annotation { "Feature Type Name" : "Feature", "Feature Type Description" : "" }
export const myFeature = defineFeature(function(context is Context, id is Id, definition is map)
    precondition{}
    {
        {
            var Q0;
            Q0=qCreatedBy(makeId("Top.planeOp"),FACE);
            var sketch = newSketch(context, id + "F0", { "sketchPlane" : qUnion([Q0])});
            skLineSegment(sketch, "E0.bottom", {"start": v(60, 20) * mm, "end": v(-60, 20) * mm});
            skLineSegment(sketch, "E0.top", {"start": v(60, -20) * mm, "end": v(-60, -20) * mm});
            skLineSegment(sketch, "E0.left", {"start": v(60, 20) * mm, "end": v(60, -20) * mm});
            skLineSegment(sketch, "E0.right", {"start": v(-60, 20) * mm, "end": v(-60, -20) * mm});
            skPoint(sketch, "E0.middle", {"position": v(0, 0) * mm});
            skText(sketch, "E1", { "text": "Ingvar Lohoff", "fontName": "RobotoSlab-Regular.ttf"});
            skText(sketch, "E2", { "text": "R&D Technician", "fontName": "OpenSans-Italic.ttf"});
            skLineSegment(sketch, "E3.bottom", {"start": v(-58.5, 18.5) * mm, "end": v(58.5, 18.5) * mm});
            skLineSegment(sketch, "E3.top", {"start": v(-58.5, -18.5) * mm, "end": v(58.5, -18.5) * mm});
            skLineSegment(sketch, "E3.left", {"start": v(-58.5, 18.5) * mm, "end": v(-58.5, -18.5) * mm});
            skLineSegment(sketch, "E3.right", {"start": v(58.5, 18.5) * mm, "end": v(58.5, -18.5) * mm});
            skFitSpline(sketch, "E4", {"points": [v(-37.01, -2.26) * mm, v(-45.57, -1.1) * mm], "startDerivative": vector(-15.1, -4.8) * mm, "endDerivative": vector(-4.95, 1.06) * mm});
            skFitSpline(sketch, "E5", {"points": [v(-45.57, -1.1) * mm, v(-45.12, -4.95) * mm], "startDerivative": vector(-3.78, -1.31) * mm, "endDerivative": vector(-0.25, -3.22) * mm});
            skLineSegment(sketch, "E6", {"start": v(-47.57, -11.95) * mm, "end": v(-48.94, -11.95) * mm});
            skFitSpline(sketch, "E7", {"points": [v(-48.94, -11.95) * mm, v(-51.13, -11.8) * mm], "startDerivative": vector(-2.81, -1.67) * mm, "endDerivative": vector(-2.2, 0.14) * mm});
            skLineSegment(sketch, "E8", {"start": v(-51.13, -11.8) * mm, "end": v(-52.08, -11.76) * mm});
            skFitSpline(sketch, "E9", {"points": [v(-52.08, -11.76) * mm, v(-52.08, -10.55) * mm], "startDerivative": vector(-0.1, 0.28) * mm, "endDerivative": vector(2.07, 2.15) * mm});
            skFitSpline(sketch, "E10", {"points": [v(-52.08, -10.55) * mm, v(-49.92, -8.8) * mm], "startDerivative": vector(0, 2.8) * mm, "endDerivative": vector(5.06, 0.12) * mm});
            skFitSpline(sketch, "E11", {"points": [v(-49.92, -8.8) * mm, v(-48.55, -6.8) * mm], "startDerivative": vector(1.37, 2) * mm, "endDerivative": vector(0.03, 3.47) * mm});
            skLineSegment(sketch, "E12", {"start": v(-48.55, -6.8) * mm, "end": v(-49.5, -4.88) * mm});
            skLineSegment(sketch, "E13", {"start": v(-49.5, -4.88) * mm, "end": v(-49.6, -3.78) * mm});
            skLineSegment(sketch, "E14", {"start": v(-49.6, -3.78) * mm, "end": v(-50.42, -1.31) * mm});
            skLineSegment(sketch, "E15", {"start": v(-50.42, -1.31) * mm, "end": v(-50.35, -0.53) * mm});
            skFitSpline(sketch, "E16", {"points": [v(-50.35, -0.53) * mm, v(-50.45, 2.82) * mm], "startDerivative": vector(3.53, 5.18) * mm, "endDerivative": vector(-0.39, 3.2) * mm});
            skFitSpline(sketch, "E17", {"points": [v(-50.45, 2.82) * mm, v(-49.19, 7.14) * mm], "startDerivative": vector(-0.01, 2.66) * mm, "endDerivative": vector(0.34, 7.24) * mm});
            skFitSpline(sketch, "E18", {"points": [v(-49.19, 7.14) * mm, v(-46.94, 9.2) * mm], "startDerivative": vector(0.56, 2.02) * mm, "endDerivative": vector(1.5, 2.36) * mm});
            skFitSpline(sketch, "E19", {"points": [v(-46.94, 9.2) * mm, v(-47.8, 8.97) * mm], "startDerivative": vector(0.03, 0.36) * mm, "endDerivative": vector(-2.54, -1.89) * mm});
            skLineSegment(sketch, "E20", {"start": v(-47.8, 8.97) * mm, "end": v(-48.16, 8.97) * mm});
            skLineSegment(sketch, "E21", {"start": v(-48.16, 8.97) * mm, "end": v(-48.43, 9.62) * mm});
            skLineSegment(sketch, "E22", {"start": v(-48.43, 9.62) * mm, "end": v(-48.43, 10.25) * mm});
            skLineSegment(sketch, "E23", {"start": v(-48.43, 10.25) * mm, "end": v(-48.9, 11.06) * mm});
            skLineSegment(sketch, "E24", {"start": v(-48.9, 11.06) * mm, "end": v(-48.9, 11.38) * mm});
            skLineSegment(sketch, "E25", {"start": v(-48.9, 11.38) * mm, "end": v(-48.16, 11.92) * mm});
            skLineSegment(sketch, "E26", {"start": v(-48.16, 11.92) * mm, "end": v(-47.8, 13.18) * mm});
            skLineSegment(sketch, "E27", {"start": v(-47.8, 13.18) * mm, "end": v(-47.22, 13.34) * mm});
            skLineSegment(sketch, "E28", {"start": v(-47.22, 13.34) * mm, "end": v(-46.88, 13.58) * mm});
            skLineSegment(sketch, "E29", {"start": v(-46.88, 13.58) * mm, "end": v(-46.19, 14.23) * mm});
            skLineSegment(sketch, "E30", {"start": v(-46.19, 14.23) * mm, "end": v(-43.13, 14.23) * mm});
            skLineSegment(sketch, "E31", {"start": v(-35.33, 13.67) * mm, "end": v(-35.03, 13.25) * mm});
            skLineSegment(sketch, "E32", {"start": v(-35.03, 13.25) * mm, "end": v(-34.67, 13.19) * mm});
            skLineSegment(sketch, "E33", {"start": v(-34.67, 13.19) * mm, "end": v(-34.35, 13.23) * mm});
            skLineSegment(sketch, "E34", {"start": v(-34.35, 13.23) * mm, "end": v(-33.33, 13.42) * mm});
            skLineSegment(sketch, "E35", {"start": v(-33.33, 13.42) * mm, "end": v(-31.66, 13.42) * mm});
            skLineSegment(sketch, "E36", {"start": v(-31.66, 13.42) * mm, "end": v(-28.02, 12.26) * mm});
            skLineSegment(sketch, "E37", {"start": v(-28.02, 12.26) * mm, "end": v(-27.07, 11.46) * mm});
            skLineSegment(sketch, "E38", {"start": v(-27.07, 11.46) * mm, "end": v(-24.98, 8.2) * mm});
            skFitSpline(sketch, "E39", {"points": [v(-24.98, 8.2) * mm, v(-23.42, 3.5) * mm], "startDerivative": vector(1.95, -5.48) * mm, "endDerivative": vector(0.76, -4.65) * mm});
            skFitSpline(sketch, "E40", {"points": [v(-23.42, 3.5) * mm, v(-21.37, -1.43) * mm], "startDerivative": vector(7.6, -13.42) * mm, "endDerivative": vector(4.61, -7.58) * mm});
            skFitSpline(sketch, "E41", {"points": [v(-21.37, -1.43) * mm, v(-19.72, -5.6) * mm], "startDerivative": vector(1.54, -4.41) * mm, "endDerivative": vector(4.95, -6.29) * mm});
            skFitSpline(sketch, "E42", {"points": [v(-19.72, -5.6) * mm, v(-18.43, -8.78) * mm], "startDerivative": vector(0.4, -2.46) * mm, "endDerivative": vector(3.09, -5.04) * mm});
            skLineSegment(sketch, "E43", {"start": v(-18.43, -8.78) * mm, "end": v(-18.5, -10.05) * mm});
            skLineSegment(sketch, "E44", {"start": v(-18.5, -10.05) * mm, "end": v(-20.04, -11.11) * mm});
            skLineSegment(sketch, "E45", {"start": v(-20.04, -11.11) * mm, "end": v(-23, -11.21) * mm});
            skLineSegment(sketch, "E46", {"start": v(-23, -11.21) * mm, "end": v(-23.24, -9.38) * mm});
            skLineSegment(sketch, "E47", {"start": v(-23.24, -9.38) * mm, "end": v(-22.35, -8.01) * mm});
            skLineSegment(sketch, "E48", {"start": v(-22.35, -8.01) * mm, "end": v(-23.07, -5.52) * mm});
            skLineSegment(sketch, "E49", {"start": v(-23.07, -5.52) * mm, "end": v(-26.21, -1.7) * mm});
            skLineSegment(sketch, "E50", {"start": v(-26.21, -1.7) * mm, "end": v(-27.14, 0.18) * mm});
            skLineSegment(sketch, "E51", {"start": v(-27.14, 0.18) * mm, "end": v(-28.46, 0.91) * mm});
            skLineSegment(sketch, "E52", {"start": v(-28.46, 0.91) * mm, "end": v(-28.85, 0.9) * mm});
            skLineSegment(sketch, "E53", {"start": v(-28.85, 0.9) * mm, "end": v(-29.89, 0.29) * mm});
            skLineSegment(sketch, "E54", {"start": v(-29.89, 0.29) * mm, "end": v(-30.62, -1.72) * mm});
            skLineSegment(sketch, "E55", {"start": v(-30.62, -1.72) * mm, "end": v(-30.02, -2.43) * mm});
            skLineSegment(sketch, "E56", {"start": v(-30.02, -2.43) * mm, "end": v(-30.02, -2.87) * mm});
            skLineSegment(sketch, "E57", {"start": v(-30.02, -2.87) * mm, "end": v(-29.18, -3.8) * mm});
            skLineSegment(sketch, "E58", {"start": v(-29.18, -3.8) * mm, "end": v(-29.18, -4.83) * mm});
            skLineSegment(sketch, "E59", {"start": v(-29.18, -4.83) * mm, "end": v(-29.37, -5.01) * mm});
            skLineSegment(sketch, "E60", {"start": v(-29.37, -5.01) * mm, "end": v(-29.54, -6.85) * mm});
            skLineSegment(sketch, "E61", {"start": v(-29.54, -6.85) * mm, "end": v(-30, -7.7) * mm});
            skLineSegment(sketch, "E62", {"start": v(-30, -7.7) * mm, "end": v(-29.9, -9.17) * mm});
            skLineSegment(sketch, "E63", {"start": v(-29.9, -9.17) * mm, "end": v(-30.36, -9.8) * mm});
            skLineSegment(sketch, "E64", {"start": v(-30.36, -9.8) * mm, "end": v(-31.5, -10.15) * mm});
            skLineSegment(sketch, "E65", {"start": v(-31.5, -10.15) * mm, "end": v(-32.6, -9.99) * mm});
            skLineSegment(sketch, "E66", {"start": v(-32.6, -9.99) * mm, "end": v(-33.43, -9.99) * mm});
            skLineSegment(sketch, "E67", {"start": v(-33.43, -9.99) * mm, "end": v(-34.14, -9.3) * mm});
            skLineSegment(sketch, "E68", {"start": v(-34.14, -9.3) * mm, "end": v(-33.43, -7.58) * mm});
            skLineSegment(sketch, "E69", {"start": v(-33.43, -7.58) * mm, "end": v(-32.46, -7.58) * mm});
            skLineSegment(sketch, "E70", {"start": v(-32.46, -7.58) * mm, "end": v(-32.19, -5.74) * mm});
            skLineSegment(sketch, "E71", {"start": v(-32.19, -5.74) * mm, "end": v(-32.76, -5.32) * mm});
            skLineSegment(sketch, "E72", {"start": v(-32.76, -5.32) * mm, "end": v(-34.18, -7.89) * mm});
            skLineSegment(sketch, "E73", {"start": v(-34.18, -7.89) * mm, "end": v(-34.42, -9.19) * mm});
            skLineSegment(sketch, "E74", {"start": v(-34.42, -9.19) * mm, "end": v(-34.42, -9.74) * mm});
            skLineSegment(sketch, "E75", {"start": v(-34.42, -9.74) * mm, "end": v(-33.64, -10.38) * mm});
            skLineSegment(sketch, "E76", {"start": v(-33.64, -10.38) * mm, "end": v(-32.13, -11.4) * mm});
            skLineSegment(sketch, "E77", {"start": v(-32.13, -11.4) * mm, "end": v(-32.13, -12.56) * mm});
            skLineSegment(sketch, "E78", {"start": v(-32.13, -12.56) * mm, "end": v(-33.27, -14.18) * mm});
            skLineSegment(sketch, "E79", {"start": v(-33.27, -14.18) * mm, "end": v(-35.5, -14.44) * mm});
            skLineSegment(sketch, "E80", {"start": v(-35.5, -14.44) * mm, "end": v(-35.98, -14.18) * mm});
            skLineSegment(sketch, "E81", {"start": v(-35.98, -14.18) * mm, "end": v(-37.5, -13.5) * mm});
            skLineSegment(sketch, "E82", {"start": v(-37.5, -13.5) * mm, "end": v(-37.82, -12.88) * mm});
            skLineSegment(sketch, "E83", {"start": v(-37.82, -12.88) * mm, "end": v(-37.82, -12.24) * mm});
            skLineSegment(sketch, "E84", {"start": v(-37.82, -12.24) * mm, "end": v(-37.5, -11.63) * mm});
            skLineSegment(sketch, "E85", {"start": v(-37.5, -11.63) * mm, "end": v(-37.4, -10.76) * mm});
            skLineSegment(sketch, "E86", {"start": v(-37.4, -10.76) * mm, "end": v(-37.56, -9.52) * mm});
            skLineSegment(sketch, "E87", {"start": v(-37.56, -9.52) * mm, "end": v(-36.92, -7.9) * mm});
            skLineSegment(sketch, "E88", {"start": v(-36.92, -7.9) * mm, "end": v(-36.84, -6.34) * mm});
            skLineSegment(sketch, "E89", {"start": v(-36.84, -6.34) * mm, "end": v(-36.77, -5.62) * mm});
            skLineSegment(sketch, "E90", {"start": v(-36.77, -5.62) * mm, "end": v(-37.17, -4.96) * mm});
            skLineSegment(sketch, "E91", {"start": v(-37.17, -4.96) * mm, "end": v(-37.17, -4.12) * mm});
            skLineSegment(sketch, "E92", {"start": v(-37.17, -4.12) * mm, "end": v(-36.85, -3.72) * mm});
            skLineSegment(sketch, "E93", {"start": v(-36.85, -3.72) * mm, "end": v(-37.01, -2.26) * mm});
            skFitSpline(sketch, "E94", {"points": [v(-43.06, 8.26) * mm, v(-44.01, 2.88) * mm], "startDerivative": vector(-1.63, -3.33) * mm, "endDerivative": vector(-1.14, -3.3) * mm});
            skFitSpline(sketch, "E95", {"points": [v(-43.06, 8.26) * mm, v(-44.01, 2.88) * mm], "startDerivative": vector(-0.47, -0.16) * mm, "endDerivative": vector(3.55, -12.32) * mm});
            skLineSegment(sketch, "E96", {"start": v(-49.48, -9.26) * mm, "end": v(-49.81, -10.61) * mm});
            skLineSegment(sketch, "E97", {"start": v(-49.81, -10.61) * mm, "end": v(-48.9, -10.75) * mm});
            skLineSegment(sketch, "E98", {"start": v(-48.9, -10.75) * mm, "end": v(-48.55, -11.05) * mm});
            skLineSegment(sketch, "E99", {"start": v(-48.55, -11.05) * mm, "end": v(-48, -10.75) * mm});
            skLineSegment(sketch, "E100", {"start": v(-48, -10.75) * mm, "end": v(-47.64, -10.49) * mm});
            skLineSegment(sketch, "E101", {"start": v(-47.64, -10.49) * mm, "end": v(-47.32, -10.16) * mm});
            skLineSegment(sketch, "E102", {"start": v(-47.32, -10.16) * mm, "end": v(-47.04, -9.8) * mm});
            skLineSegment(sketch, "E103", {"start": v(-47.04, -9.8) * mm, "end": v(-46.73, -9.47) * mm});
            skLineSegment(sketch, "E104", {"start": v(-46.73, -9.47) * mm, "end": v(-46.88, -8.9) * mm});
            skLineSegment(sketch, "E105", {"start": v(-46.88, -8.9) * mm, "end": v(-46.27, -7.92) * mm});
            skLineSegment(sketch, "E106", {"start": v(-46.27, -7.92) * mm, "end": v(-46.23, -7.25) * mm});
            skLineSegment(sketch, "E107", {"start": v(-46.23, -7.25) * mm, "end": v(-47.11, -5.57) * mm});
            skLineSegment(sketch, "E108", {"start": v(-47.11, -5.57) * mm, "end": v(-47.16, -4.63) * mm});
            skLineSegment(sketch, "E109", {"start": v(-47.16, -4.63) * mm, "end": v(-46.67, -5.47) * mm});
            skLineSegment(sketch, "E110", {"start": v(-46.67, -5.47) * mm, "end": v(-46.34, -4.87) * mm});
            skLineSegment(sketch, "E111", {"start": v(-46.34, -4.87) * mm, "end": v(-46.34, -3.88) * mm});
            skLineSegment(sketch, "E112", {"start": v(-46.34, -3.88) * mm, "end": v(-46.54, -3.11) * mm});
            skLineSegment(sketch, "E113", {"start": v(-46.54, -3.11) * mm, "end": v(-47, -2.56) * mm});
            skLineSegment(sketch, "E114", {"start": v(-47, -2.56) * mm, "end": v(-48.65, -1.21) * mm});
            skLineSegment(sketch, "E115", {"start": v(-48.65, -1.21) * mm, "end": v(-48.65, -2.55) * mm});
            skLineSegment(sketch, "E116", {"start": v(-48.65, -2.55) * mm, "end": v(-48.11, -4.64) * mm});
            skLineSegment(sketch, "E117", {"start": v(-48.11, -4.64) * mm, "end": v(-47.39, -6.06) * mm});
            skLineSegment(sketch, "E118", {"start": v(-47.39, -6.06) * mm, "end": v(-48.11, -4.64) * mm});
            skLineSegment(sketch, "E119", {"start": v(-48.11, -4.64) * mm, "end": v(-47.97, -6.35) * mm});
            skLineSegment(sketch, "E120", {"start": v(-47.97, -6.35) * mm, "end": v(-47.53, -7.91) * mm});
            skLineSegment(sketch, "E121", {"start": v(-47.5, -7.92) * mm, "end": v(-47.53, -7.91) * mm});
            skLineSegment(sketch, "E122", {"start": v(-47.5, -7.92) * mm, "end": v(-48.15, -7.92) * mm});
            skLineSegment(sketch, "E123", {"start": v(-48.15, -7.92) * mm, "end": v(-48.5, -8.2) * mm});
            skLineSegment(sketch, "E124", {"start": v(-48.5, -8.2) * mm, "end": v(-48.58, -8.91) * mm});
            skLineSegment(sketch, "E125", {"start": v(-48.58, -8.91) * mm, "end": v(-48.88, -9.23) * mm});
            skLineSegment(sketch, "E126", {"start": v(-48.88, -9.23) * mm, "end": v(-49.48, -9.26) * mm});
            skLineSegment(sketch, "E127", {"start": v(-42.25, 6.43) * mm, "end": v(-42.61, 7.08) * mm});
            skLineSegment(sketch, "E128", {"start": v(-42.61, 7.08) * mm, "end": v(-43.15, 5.63) * mm});
            skLineSegment(sketch, "E129", {"start": v(-43.15, 5.63) * mm, "end": v(-43.15, 5.36) * mm});
            skLineSegment(sketch, "E130", {"start": v(-43.15, 5.36) * mm, "end": v(-42.73, 5.37) * mm});
            skLineSegment(sketch, "E131", {"start": v(-42.73, 5.37) * mm, "end": v(-41.17, 6) * mm});
            skLineSegment(sketch, "E132", {"start": v(-41.17, 6) * mm, "end": v(-40.31, 5.94) * mm});
            skLineSegment(sketch, "E133", {"start": v(-40.31, 5.94) * mm, "end": v(-39.61, 4.96) * mm});
            skLineSegment(sketch, "E134", {"start": v(-39.61, 4.96) * mm, "end": v(-39.53, 4.51) * mm});
            skLineSegment(sketch, "E135", {"start": v(-39.53, 4.51) * mm, "end": v(-39.35, 4.34) * mm});
            skLineSegment(sketch, "E136", {"start": v(-39.35, 4.34) * mm, "end": v(-38.96, 4.38) * mm});
            skLineSegment(sketch, "E137", {"start": v(-38.96, 4.38) * mm, "end": v(-38.83, 4.58) * mm});
            skLineSegment(sketch, "E138", {"start": v(-38.83, 4.58) * mm, "end": v(-39.03, 5.47) * mm});
            skLineSegment(sketch, "E139", {"start": v(-39.03, 5.47) * mm, "end": v(-39.03, 7.07) * mm});
            skLineSegment(sketch, "E140", {"start": v(-39.03, 7.07) * mm, "end": v(-38.53, 5.9) * mm});
            skLineSegment(sketch, "E141", {"start": v(-38.53, 5.9) * mm, "end": v(-38.53, 4.87) * mm});
            skLineSegment(sketch, "E142", {"start": v(-38.53, 4.87) * mm, "end": v(-38.4, 3.45) * mm});
            skLineSegment(sketch, "E143", {"start": v(-38.4, 3.45) * mm, "end": v(-38.66, 2.53) * mm});
            skLineSegment(sketch, "E144", {"start": v(-38.66, 2.53) * mm, "end": v(-38.24, 2.41) * mm});
            skLineSegment(sketch, "E145", {"start": v(-38.24, 2.41) * mm, "end": v(-37.71, 2.87) * mm});
            skLineSegment(sketch, "E146", {"start": v(-37.71, 2.87) * mm, "end": v(-37.6, 4.48) * mm});
            skLineSegment(sketch, "E147", {"start": v(-37.6, 4.48) * mm, "end": v(-37.83, 5.13) * mm});
            skLineSegment(sketch, "E148", {"start": v(-37.83, 5.13) * mm, "end": v(-37.83, 6.51) * mm});
            skLineSegment(sketch, "E149", {"start": v(-37.83, 6.51) * mm, "end": v(-38.5, 8.28) * mm});
            skLineSegment(sketch, "E150", {"start": v(-38.5, 8.28) * mm, "end": v(-38.82, 8.28) * mm});
            skLineSegment(sketch, "E151", {"start": v(-38.82, 8.28) * mm, "end": v(-38.88, 8) * mm});
            skLineSegment(sketch, "E152", {"start": v(-38.88, 8) * mm, "end": v(-39.33, 8.34) * mm});
            skLineSegment(sketch, "E153", {"start": v(-39.33, 8.34) * mm, "end": v(-40.16, 8.69) * mm});
            skLineSegment(sketch, "E154", {"start": v(-40.16, 8.69) * mm, "end": v(-40.5, 9.3) * mm});
            skLineSegment(sketch, "E155", {"start": v(-40.5, 9.3) * mm, "end": v(-40.95, 9.3) * mm});
            skLineSegment(sketch, "E156", {"start": v(-40.95, 9.3) * mm, "end": v(-41.14, 9.21) * mm});
            skLineSegment(sketch, "E157", {"start": v(-41.14, 9.21) * mm, "end": v(-41.6, 9.37) * mm});
            skLineSegment(sketch, "E158", {"start": v(-41.6, 9.37) * mm, "end": v(-42.18, 9.03) * mm});
            skLineSegment(sketch, "E159", {"start": v(-42.18, 9.03) * mm, "end": v(-42.13, 8.67) * mm});
            skLineSegment(sketch, "E160", {"start": v(-42.13, 8.67) * mm, "end": v(-41.76, 8.77) * mm});
            skLineSegment(sketch, "E161", {"start": v(-41.76, 8.77) * mm, "end": v(-42.24, 8.14) * mm});
            skLineSegment(sketch, "E162", {"start": v(-42.24, 8.14) * mm, "end": v(-42.24, 7.74) * mm});
            skLineSegment(sketch, "E163", {"start": v(-42.24, 7.74) * mm, "end": v(-41.77, 7.79) * mm});
            skLineSegment(sketch, "E164", {"start": v(-41.77, 7.79) * mm, "end": v(-41.65, 8.17) * mm});
            skLineSegment(sketch, "E165", {"start": v(-41.65, 8.17) * mm, "end": v(-41.4, 8.2) * mm});
            skLineSegment(sketch, "E166", {"start": v(-41.4, 8.2) * mm, "end": v(-41.38, 7.56) * mm});
            skLineSegment(sketch, "E167", {"start": v(-41.38, 7.56) * mm, "end": v(-41.43, 6.8) * mm});
            skLineSegment(sketch, "E168", {"start": v(-41.43, 6.8) * mm, "end": v(-40.18, 6.56) * mm});
            skLineSegment(sketch, "E169", {"start": v(-40.18, 6.56) * mm, "end": v(-39.03, 5.47) * mm});
            skLineSegment(sketch, "E170", {"start": v(-42.25, 6.43) * mm, "end": v(-41.43, 6.8) * mm});
            skLineSegment(sketch, "E171", {"start": v(-45.52, 9.79) * mm, "end": v(-45.52, 9.2) * mm});
            skLineSegment(sketch, "E172", {"start": v(-45.52, 9.2) * mm, "end": v(-45.08, 9.2) * mm});
            skLineSegment(sketch, "E173", {"start": v(-45.08, 9.2) * mm, "end": v(-44.28, 9.84) * mm});
            skLineSegment(sketch, "E174", {"start": v(-44.28, 9.84) * mm, "end": v(-43.77, 9.82) * mm});
            skLineSegment(sketch, "E175", {"start": v(-43.77, 9.82) * mm, "end": v(-42.83, 9.73) * mm});
            skLineSegment(sketch, "E176", {"start": v(-42.83, 9.73) * mm, "end": v(-42.25, 10.15) * mm});
            skLineSegment(sketch, "E177", {"start": v(-42.25, 10.15) * mm, "end": v(-41.87, 11.3) * mm});
            skLineSegment(sketch, "E178", {"start": v(-41.87, 11.3) * mm, "end": v(-43.08, 11.36) * mm});
            skLineSegment(sketch, "E179", {"start": v(-43.08, 11.36) * mm, "end": v(-43.86, 11.03) * mm});
            skLineSegment(sketch, "E180", {"start": v(-43.86, 11.03) * mm, "end": v(-44.72, 9.96) * mm});
            skLineSegment(sketch, "E181", {"start": v(-44.72, 9.96) * mm, "end": v(-45.05, 9.68) * mm});
            skLineSegment(sketch, "E182", {"start": v(-45.05, 9.68) * mm, "end": v(-45.52, 9.79) * mm});
            skLineSegment(sketch, "E183", {"start": v(-41.6, 11.23) * mm, "end": v(-40.84, 11.48) * mm});
            skLineSegment(sketch, "E184", {"start": v(-40.84, 11.48) * mm, "end": v(-40.65, 11.25) * mm});
            skLineSegment(sketch, "E185", {"start": v(-40.65, 11.25) * mm, "end": v(-40.59, 10.48) * mm});
            skLineSegment(sketch, "E186", {"start": v(-40.59, 10.48) * mm, "end": v(-40.87, 10.14) * mm});
            skLineSegment(sketch, "E187", {"start": v(-40.87, 10.14) * mm, "end": v(-40.95, 9.64) * mm});
            skLineSegment(sketch, "E188", {"start": v(-40.95, 9.64) * mm, "end": v(-41.3, 9.56) * mm});
            skLineSegment(sketch, "E189", {"start": v(-41.3, 9.56) * mm, "end": v(-41.8, 10.3) * mm});
            skLineSegment(sketch, "E190", {"start": v(-41.8, 10.3) * mm, "end": v(-41.6, 11.23) * mm});
            skLineSegment(sketch, "E191", {"start": v(-40.16, 8.69) * mm, "end": v(-39.8, 9.55) * mm});
            skLineSegment(sketch, "E192", {"start": v(-39.8, 9.55) * mm, "end": v(-39, 9.64) * mm});
            skLineSegment(sketch, "E193", {"start": v(-39, 9.64) * mm, "end": v(-38.5, 8.28) * mm});
            skLineSegment(sketch, "E194", {"start": v(-35.8, 13.16) * mm, "end": v(-36.19, 13.57) * mm});
            skLineSegment(sketch, "E195", {"start": v(-36.19, 13.57) * mm, "end": v(-36.62, 13.92) * mm});
            skLineSegment(sketch, "E196", {"start": v(-36.62, 13.92) * mm, "end": v(-37.34, 13.87) * mm});
            skLineSegment(sketch, "E197", {"start": v(-37.34, 13.87) * mm, "end": v(-38, 13.78) * mm});
            skLineSegment(sketch, "E198", {"start": v(-38, 13.78) * mm, "end": v(-38.9, 13.76) * mm});
            skLineSegment(sketch, "E199", {"start": v(-38.9, 13.76) * mm, "end": v(-39.68, 14.06) * mm});
            skLineSegment(sketch, "E200", {"start": v(-39.68, 14.06) * mm, "end": v(-40.49, 14) * mm});
            skLineSegment(sketch, "E201", {"start": v(-40.49, 14) * mm, "end": v(-41.44, 13.7) * mm});
            skLineSegment(sketch, "E202", {"start": v(-41.44, 13.7) * mm, "end": v(-42.84, 13.76) * mm});
            skLineSegment(sketch, "E203", {"start": v(-42.84, 13.76) * mm, "end": v(-44.02, 13.65) * mm});
            skLineSegment(sketch, "E204", {"start": v(-44.02, 13.65) * mm, "end": v(-44.01, 13.53) * mm});
            skLineSegment(sketch, "E205", {"start": v(-44.01, 13.53) * mm, "end": v(-42.91, 13.45) * mm});
            skLineSegment(sketch, "E206", {"start": v(-42.91, 13.45) * mm, "end": v(-41.9, 13.08) * mm});
            skLineSegment(sketch, "E207", {"start": v(-41.9, 13.08) * mm, "end": v(-41.23, 12.96) * mm});
            skLineSegment(sketch, "E208", {"start": v(-41.23, 12.96) * mm, "end": v(-39.58, 13.33) * mm});
            skLineSegment(sketch, "E209", {"start": v(-39.58, 13.33) * mm, "end": v(-38.84, 13.3) * mm});
            skLineSegment(sketch, "E210", {"start": v(-38.84, 13.3) * mm, "end": v(-38.76, 13.12) * mm});
            skLineSegment(sketch, "E211", {"start": v(-38.76, 13.12) * mm, "end": v(-39.8, 13.07) * mm});
            skLineSegment(sketch, "E212", {"start": v(-39.8, 13.07) * mm, "end": v(-40.9, 12.78) * mm});
            skLineSegment(sketch, "E213", {"start": v(-40.9, 12.78) * mm, "end": v(-42.07, 12.84) * mm});
            skLineSegment(sketch, "E214", {"start": v(-42.07, 12.84) * mm, "end": v(-43.32, 13.1) * mm});
            skLineSegment(sketch, "E215", {"start": v(-43.32, 13.1) * mm, "end": v(-43.74, 13.1) * mm});
            skLineSegment(sketch, "E216", {"start": v(-43.74, 13.1) * mm, "end": v(-44.49, 12.9) * mm});
            skLineSegment(sketch, "E217", {"start": v(-44.49, 12.9) * mm, "end": v(-44.95, 12) * mm});
            skLineSegment(sketch, "E218", {"start": v(-44.95, 12) * mm, "end": v(-44.77, 11.9) * mm});
            skLineSegment(sketch, "E219", {"start": v(-44.77, 11.9) * mm, "end": v(-43.85, 12.63) * mm});
            skLineSegment(sketch, "E220", {"start": v(-43.85, 12.63) * mm, "end": v(-42.45, 12.52) * mm});
            skLineSegment(sketch, "E221", {"start": v(-42.45, 12.52) * mm, "end": v(-40.95, 12.52) * mm});
            skLineSegment(sketch, "E222", {"start": v(-40.95, 12.52) * mm, "end": v(-40.94, 12.42) * mm});
            skLineSegment(sketch, "E223", {"start": v(-40.94, 12.42) * mm, "end": v(-42.95, 11.84) * mm});
            skLineSegment(sketch, "E224", {"start": v(-42.95, 11.84) * mm, "end": v(-42.95, 11.69) * mm});
            skLineSegment(sketch, "E225", {"start": v(-42.95, 11.69) * mm, "end": v(-40, 11.68) * mm});
            skLineSegment(sketch, "E226", {"start": v(-40, 11.68) * mm, "end": v(-39.85, 11.58) * mm});
            skLineSegment(sketch, "E227", {"start": v(-39.85, 11.58) * mm, "end": v(-40.3, 11.25) * mm});
            skLineSegment(sketch, "E228", {"start": v(-40.3, 11.25) * mm, "end": v(-40.38, 10.24) * mm});
            skLineSegment(sketch, "E229", {"start": v(-40.38, 10.24) * mm, "end": v(-40.13, 9.83) * mm});
            skLineSegment(sketch, "E230", {"start": v(-40.13, 9.83) * mm, "end": v(-39.44, 9.74) * mm});
            skLineSegment(sketch, "E231", {"start": v(-39.44, 9.74) * mm, "end": v(-38.03, 10.4) * mm});
            skLineSegment(sketch, "E232", {"start": v(-38.03, 10.4) * mm, "end": v(-38.07, 9.85) * mm});
            skLineSegment(sketch, "E233", {"start": v(-38.07, 9.85) * mm, "end": v(-37.85, 9.66) * mm});
            skLineSegment(sketch, "E234", {"start": v(-37.85, 9.66) * mm, "end": v(-37, 9.88) * mm});
            skLineSegment(sketch, "E235", {"start": v(-37, 9.88) * mm, "end": v(-37.26, 9.28) * mm});
            skLineSegment(sketch, "E236", {"start": v(-37.26, 9.28) * mm, "end": v(-37.1, 8.78) * mm});
            skLineSegment(sketch, "E237", {"start": v(-37.1, 8.78) * mm, "end": v(-37.1, 8.28) * mm});
            skLineSegment(sketch, "E238", {"start": v(-37.1, 8.28) * mm, "end": v(-37.19, 8.32) * mm});
            skLineSegment(sketch, "E239", {"start": v(-37.19, 8.32) * mm, "end": v(-37.3, 8.92) * mm});
            skLineSegment(sketch, "E240", {"start": v(-37.3, 8.92) * mm, "end": v(-37.72, 9.16) * mm});
            skLineSegment(sketch, "E241", {"start": v(-37.72, 9.16) * mm, "end": v(-38.13, 8.96) * mm});
            skLineSegment(sketch, "E242", {"start": v(-38.13, 8.96) * mm, "end": v(-38.13, 8.08) * mm});
            skLineSegment(sketch, "E243", {"start": v(-38.13, 8.08) * mm, "end": v(-37.51, 6.75) * mm});
            skLineSegment(sketch, "E244", {"start": v(-37.51, 6.75) * mm, "end": v(-37.24, 4.7) * mm});
            skLineSegment(sketch, "E245", {"start": v(-37.24, 4.7) * mm, "end": v(-36.86, 5.24) * mm});
            skLineSegment(sketch, "E246", {"start": v(-36.86, 5.24) * mm, "end": v(-36.86, 6.1) * mm});
            skLineSegment(sketch, "E247", {"start": v(-36.86, 6.1) * mm, "end": v(-36.28, 7.23) * mm});
            skLineSegment(sketch, "E248", {"start": v(-36.28, 7.23) * mm, "end": v(-36.25, 9.68) * mm});
            skLineSegment(sketch, "E249", {"start": v(-36.25, 9.68) * mm, "end": v(-38.08, 11.36) * mm});
            skLineSegment(sketch, "E250", {"start": v(-38.08, 11.36) * mm, "end": v(-38.44, 12.69) * mm});
            skLineSegment(sketch, "E251", {"start": v(-38.44, 12.69) * mm, "end": v(-37.78, 11.88) * mm});
            skLineSegment(sketch, "E252", {"start": v(-37.78, 11.88) * mm, "end": v(-36.99, 12.76) * mm});
            skLineSegment(sketch, "E253", {"start": v(-36.99, 12.76) * mm, "end": v(-37.25, 13.55) * mm});
            skLineSegment(sketch, "E254", {"start": v(-37.25, 13.55) * mm, "end": v(-36.42, 13.47) * mm});
            skLineSegment(sketch, "E255", {"start": v(-36.42, 13.47) * mm, "end": v(-36, 12.7) * mm});
            skLineSegment(sketch, "E256", {"start": v(-36, 12.7) * mm, "end": v(-36.01, 12.1) * mm});
            skLineSegment(sketch, "E257", {"start": v(-36.01, 12.1) * mm, "end": v(-36.64, 11.57) * mm});
            skLineSegment(sketch, "E258", {"start": v(-36.64, 11.57) * mm, "end": v(-36.38, 10.5) * mm});
            skLineSegment(sketch, "E259", {"start": v(-36.38, 10.5) * mm, "end": v(-35.9, 9.8) * mm});
            skLineSegment(sketch, "E260", {"start": v(-35.9, 9.8) * mm, "end": v(-35.35, 10.11) * mm});
            skLineSegment(sketch, "E261", {"start": v(-35.35, 10.11) * mm, "end": v(-35.31, 11.34) * mm});
            skLineSegment(sketch, "E262", {"start": v(-35.31, 11.34) * mm, "end": v(-35.62, 11.92) * mm});
            skLineSegment(sketch, "E263", {"start": v(-35.62, 11.92) * mm, "end": v(-35.8, 13.16) * mm});
            skLineSegment(sketch, "E264", {"start": v(-41.45, 3.22) * mm, "end": v(-42, 3.22) * mm});
            skLineSegment(sketch, "E265", {"start": v(-42, 3.22) * mm, "end": v(-42, 2.92) * mm});
            skLineSegment(sketch, "E266", {"start": v(-42, 2.92) * mm, "end": v(-41.5, 2.56) * mm});
            skLineSegment(sketch, "E267", {"start": v(-41.5, 2.56) * mm, "end": v(-41.07, 2.58) * mm});
            skLineSegment(sketch, "E268", {"start": v(-41.07, 2.58) * mm, "end": v(-41.06, 2.9) * mm});
            skLineSegment(sketch, "E269", {"start": v(-41.06, 2.9) * mm, "end": v(-41.45, 3.22) * mm});
            skLineSegment(sketch, "E270", {"start": v(-40.55, 3.92) * mm, "end": v(-40.73, 3.55) * mm});
            skLineSegment(sketch, "E271", {"start": v(-40.73, 3.55) * mm, "end": v(-40.7, 2.62) * mm});
            skLineSegment(sketch, "E272", {"start": v(-40.7, 2.62) * mm, "end": v(-40.57, 2.3) * mm});
            skLineSegment(sketch, "E273", {"start": v(-40.57, 2.3) * mm, "end": v(-40.1, 2.24) * mm});
            skLineSegment(sketch, "E274", {"start": v(-40.1, 2.24) * mm, "end": v(-39.8, 2.09) * mm});
            skLineSegment(sketch, "E275", {"start": v(-39.8, 2.09) * mm, "end": v(-39.7, 2.23) * mm});
            skLineSegment(sketch, "E276", {"start": v(-39.7, 2.23) * mm, "end": v(-40.12, 2.9) * mm});
            skLineSegment(sketch, "E277", {"start": v(-40.12, 2.9) * mm, "end": v(-40.35, 3.36) * mm});
            skLineSegment(sketch, "E278", {"start": v(-40.35, 3.36) * mm, "end": v(-40.34, 3.87) * mm});
            skLineSegment(sketch, "E279", {"start": v(-40.34, 3.87) * mm, "end": v(-40.55, 3.92) * mm});
            skLineSegment(sketch, "E280", {"start": v(-20.02, -9.49) * mm, "end": v(-20.67, -9.05) * mm});
            skLineSegment(sketch, "E281", {"start": v(-20.67, -9.05) * mm, "end": v(-21.9, -9.05) * mm});
            skLineSegment(sketch, "E282", {"start": v(-21.9, -9.05) * mm, "end": v(-21.9, -9.58) * mm});
            skLineSegment(sketch, "E283", {"start": v(-21.9, -9.58) * mm, "end": v(-21.76, -10.12) * mm});
            skLineSegment(sketch, "E284", {"start": v(-21.76, -10.12) * mm, "end": v(-20.15, -10.12) * mm});
            skLineSegment(sketch, "E285", {"start": v(-20.15, -10.12) * mm, "end": v(-19.61, -9.8) * mm});
            skLineSegment(sketch, "E286", {"start": v(-19.61, -9.8) * mm, "end": v(-19.4, -9.36) * mm});
            skLineSegment(sketch, "E287", {"start": v(-19.4, -9.36) * mm, "end": v(-19.48, -8.63) * mm});
            skLineSegment(sketch, "E288", {"start": v(-19.48, -8.63) * mm, "end": v(-20.19, -7.48) * mm});
            skLineSegment(sketch, "E289", {"start": v(-20.19, -7.48) * mm, "end": v(-21.65, -4.38) * mm});
            skLineSegment(sketch, "E290", {"start": v(-21.65, -4.38) * mm, "end": v(-22.32, -1.53) * mm});
            skLineSegment(sketch, "E291", {"start": v(-23.46, -2.42) * mm, "end": v(-23.2, -3.23) * mm});
            skLineSegment(sketch, "E292", {"start": v(-23.2, -3.23) * mm, "end": v(-22.8, -4.3) * mm});
            skLineSegment(sketch, "E293", {"start": v(-22.8, -4.3) * mm, "end": v(-22.06, -5.3) * mm});
            skLineSegment(sketch, "E294", {"start": v(-22.06, -5.3) * mm, "end": v(-22.24, -5.86) * mm});
            skLineSegment(sketch, "E295", {"start": v(-22.24, -5.86) * mm, "end": v(-21.84, -7.14) * mm});
            skLineSegment(sketch, "E296", {"start": v(-21.84, -7.14) * mm, "end": v(-21.7, -7.94) * mm});
            skLineSegment(sketch, "E297", {"start": v(-21.7, -7.94) * mm, "end": v(-20.71, -7.94) * mm});
            skLineSegment(sketch, "E298", {"start": v(-20.71, -7.94) * mm, "end": v(-20.07, -8.3) * mm});
            skLineSegment(sketch, "E299", {"start": v(-20.07, -8.3) * mm, "end": v(-20.02, -9.49) * mm});
            skLineSegment(sketch, "E300", {"start": v(-22.32, -1.53) * mm, "end": v(-23.66, 0) * mm});
            skLineSegment(sketch, "E301", {"start": v(-23.66, 0) * mm, "end": v(-24.7, 1.24) * mm});
            skLineSegment(sketch, "E302", {"start": v(-24.7, 1.24) * mm, "end": v(-25.23, 2.3) * mm});
            skLineSegment(sketch, "E303", {"start": v(-25.23, 2.3) * mm, "end": v(-24.61, 1.53) * mm});
            skLineSegment(sketch, "E304", {"start": v(-24.61, 1.53) * mm, "end": v(-23.48, 0.56) * mm});
            skLineSegment(sketch, "E305", {"start": v(-23.48, 0.56) * mm, "end": v(-23.15, 0.43) * mm});
            skLineSegment(sketch, "E306", {"start": v(-23.15, 0.43) * mm, "end": v(-23.42, 1.4) * mm});
            skLineSegment(sketch, "E307", {"start": v(-23.42, 1.4) * mm, "end": v(-23.78, 2.23) * mm});
            skLineSegment(sketch, "E308", {"start": v(-23.78, 2.23) * mm, "end": v(-24.9, 3.17) * mm});
            skLineSegment(sketch, "E309", {"start": v(-23.46, -2.42) * mm, "end": v(-25.74, -1.06) * mm});
            skLineSegment(sketch, "E310", {"start": v(-25.74, -1.06) * mm, "end": v(-26.17, 0.1) * mm});
            skLineSegment(sketch, "E311", {"start": v(-26.17, 0.1) * mm, "end": v(-26.45, 1.3) * mm});
            skLineSegment(sketch, "E312", {"start": v(-24.9, 3.17) * mm, "end": v(-25.2, 4.5) * mm});
            skLineSegment(sketch, "E313", {"start": v(-25.2, 4.5) * mm, "end": v(-25.39, 5.61) * mm});
            skLineSegment(sketch, "E314", {"start": v(-25.39, 5.61) * mm, "end": v(-25.74, 6.67) * mm});
            skLineSegment(sketch, "E315", {"start": v(-25.74, 6.67) * mm, "end": v(-26.12, 7.55) * mm});
            skLineSegment(sketch, "E316", {"start": v(-26.12, 7.55) * mm, "end": v(-26.29, 7.85) * mm});
            skLineSegment(sketch, "E317", {"start": v(-26.29, 7.85) * mm, "end": v(-26.47, 8.13) * mm});
            skLineSegment(sketch, "E318", {"start": v(-26.47, 8.13) * mm, "end": v(-26.72, 8.44) * mm});
            skLineSegment(sketch, "E319", {"start": v(-26.72, 8.44) * mm, "end": v(-27.23, 9.1) * mm});
            skLineSegment(sketch, "E320", {"start": v(-27.23, 9.1) * mm, "end": v(-27.85, 9.95) * mm});
            skLineSegment(sketch, "E321", {"start": v(-27.85, 9.95) * mm, "end": v(-28.77, 10.82) * mm});
            skLineSegment(sketch, "E322", {"start": v(-28.77, 10.82) * mm, "end": v(-30.2, 11.69) * mm});
            skLineSegment(sketch, "E323", {"start": v(-30.2, 11.69) * mm, "end": v(-31.5, 12.2) * mm});
            skLineSegment(sketch, "E324", {"start": v(-31.5, 12.2) * mm, "end": v(-32.77, 12.44) * mm});
            skLineSegment(sketch, "E325", {"start": v(-32.77, 12.44) * mm, "end": v(-34, 12.4) * mm});
            skLineSegment(sketch, "E326", {"start": v(-34, 12.4) * mm, "end": v(-34.68, 12.28) * mm});
            skLineSegment(sketch, "E327", {"start": v(-34.68, 12.28) * mm, "end": v(-34.62, 11.66) * mm});
            skLineSegment(sketch, "E328", {"start": v(-34.62, 11.66) * mm, "end": v(-34.53, 10.92) * mm});
            skLineSegment(sketch, "E329", {"start": v(-34.53, 10.92) * mm, "end": v(-34.55, 10.06) * mm});
            skLineSegment(sketch, "E330", {"start": v(-34.55, 10.06) * mm, "end": v(-34.6, 9.38) * mm});
            skLineSegment(sketch, "E331", {"start": v(-34.6, 9.38) * mm, "end": v(-35, 8.7) * mm});
            skLineSegment(sketch, "E332", {"start": v(-35, 8.7) * mm, "end": v(-35.16, 7.66) * mm});
            skLineSegment(sketch, "E333", {"start": v(-35.16, 7.66) * mm, "end": v(-34.34, 6.26) * mm});
            skLineSegment(sketch, "E334", {"start": v(-34.34, 6.26) * mm, "end": v(-35.15, 5.24) * mm});
            skLineSegment(sketch, "E335", {"start": v(-35.15, 5.24) * mm, "end": v(-35.31, 4.21) * mm});
            skLineSegment(sketch, "E336", {"start": v(-35.31, 4.21) * mm, "end": v(-35.7, 3.38) * mm});
            skLineSegment(sketch, "E337", {"start": v(-35.7, 3.38) * mm, "end": v(-34.94, 3.38) * mm});
            skLineSegment(sketch, "E338", {"start": v(-34.94, 3.38) * mm, "end": v(-34.51, 3.83) * mm});
            skLineSegment(sketch, "E339", {"start": v(-34.51, 3.83) * mm, "end": v(-34.51, 3.25) * mm});
            skLineSegment(sketch, "E340", {"start": v(-34.51, 3.25) * mm, "end": v(-35.37, 2.4) * mm});
            skLineSegment(sketch, "E341", {"start": v(-35.37, 2.4) * mm, "end": v(-36.42, 2.07) * mm});
            skLineSegment(sketch, "E342", {"start": v(-36.42, 2.07) * mm, "end": v(-35.77, 1.32) * mm});
            skLineSegment(sketch, "E343", {"start": v(-35.77, 1.32) * mm, "end": v(-35.1, 1.54) * mm});
            skLineSegment(sketch, "E344", {"start": v(-35.1, 1.54) * mm, "end": v(-34.49, 2.3) * mm});
            skLineSegment(sketch, "E345", {"start": v(-34.49, 2.3) * mm, "end": v(-34.35, 2) * mm});
            skLineSegment(sketch, "E346", {"start": v(-34.35, 2) * mm, "end": v(-33.74, 2.03) * mm});
            skLineSegment(sketch, "E347", {"start": v(-33.74, 2.03) * mm, "end": v(-34.34, 1.5) * mm});
            skLineSegment(sketch, "E348", {"start": v(-34.34, 1.5) * mm, "end": v(-34.47, 1.08) * mm});
            skLineSegment(sketch, "E349", {"start": v(-34.47, 1.08) * mm, "end": v(-35.76, 0.68) * mm});
            skLineSegment(sketch, "E350", {"start": v(-35.76, 0.68) * mm, "end": v(-36.86, 1.15) * mm});
            skLineSegment(sketch, "E351", {"start": v(-36.86, 1.15) * mm, "end": v(-38.18, 1.15) * mm});
            skLineSegment(sketch, "E352", {"start": v(-38.18, 1.15) * mm, "end": v(-39.01, 0.71) * mm});
            skLineSegment(sketch, "E353", {"start": v(-39.01, 0.71) * mm, "end": v(-39.32, 0.85) * mm});
            skLineSegment(sketch, "E354", {"start": v(-39.32, 0.85) * mm, "end": v(-38.22, 1.4) * mm});
            skLineSegment(sketch, "E355", {"start": v(-38.22, 1.4) * mm, "end": v(-37.37, 1.77) * mm});
            skLineSegment(sketch, "E356", {"start": v(-37.37, 1.77) * mm, "end": v(-36.9, 2.5) * mm});
            skLineSegment(sketch, "E357", {"start": v(-36.9, 2.5) * mm, "end": v(-36.56, 4.07) * mm});
            skLineSegment(sketch, "E358", {"start": v(-36.56, 4.07) * mm, "end": v(-35.76, 5.42) * mm});
            skLineSegment(sketch, "E359", {"start": v(-35.76, 5.42) * mm, "end": v(-36.04, 6.57) * mm});
            skLineSegment(sketch, "E360", {"start": v(-36.04, 6.57) * mm, "end": v(-36.64, 5.8) * mm});
            skLineSegment(sketch, "E361", {"start": v(-36.64, 5.8) * mm, "end": v(-36.7, 4.56) * mm});
            skLineSegment(sketch, "E362", {"start": v(-36.7, 4.56) * mm, "end": v(-37.47, 2.29) * mm});
            skLineSegment(sketch, "E363", {"start": v(-37.47, 2.29) * mm, "end": v(-38.04, 1.83) * mm});
            skLineSegment(sketch, "E364", {"start": v(-38.04, 1.83) * mm, "end": v(-38.66, 1.89) * mm});
            skLineSegment(sketch, "E365", {"start": v(-38.66, 1.89) * mm, "end": v(-39.57, 1.67) * mm});
            skLineSegment(sketch, "E366", {"start": v(-39.57, 1.67) * mm, "end": v(-40.63, 1.8) * mm});
            skLineSegment(sketch, "E367", {"start": v(-40.63, 1.8) * mm, "end": v(-41.3, 1.58) * mm});
            skLineSegment(sketch, "E368", {"start": v(-41.3, 1.58) * mm, "end": v(-42.2, 1.76) * mm});
            skLineSegment(sketch, "E369", {"start": v(-42.2, 1.76) * mm, "end": v(-43.3, 2.55) * mm});
            skLineSegment(sketch, "E370", {"start": v(-43.3, 2.55) * mm, "end": v(-43.37, 2.15) * mm});
            skLineSegment(sketch, "E371", {"start": v(-43.37, 2.15) * mm, "end": v(-43.13, 1.66) * mm});
            skLineSegment(sketch, "E372", {"start": v(-43.13, 1.66) * mm, "end": v(-42.39, 0.96) * mm});
            skLineSegment(sketch, "E373", {"start": v(-42.39, 0.96) * mm, "end": v(-41.54, 0.63) * mm});
            skLineSegment(sketch, "E374", {"start": v(-41.54, 0.63) * mm, "end": v(-42.6, 0.65) * mm});
            skLineSegment(sketch, "E375", {"start": v(-42.6, 0.65) * mm, "end": v(-43.78, 1.38) * mm});
            skLineSegment(sketch, "E376", {"start": v(-43.78, 1.38) * mm, "end": v(-44.74, 2.3) * mm});
            skLineSegment(sketch, "E377", {"start": v(-44.74, 2.3) * mm, "end": v(-46.54, 3.23) * mm});
            skLineSegment(sketch, "E378", {"start": v(-46.54, 3.23) * mm, "end": v(-46.45, 2.99) * mm});
            skLineSegment(sketch, "E379", {"start": v(-46.45, 2.99) * mm, "end": v(-45.7, 2.24) * mm});
            skLineSegment(sketch, "E380", {"start": v(-45.7, 2.24) * mm, "end": v(-45.34, 1.77) * mm});
            skLineSegment(sketch, "E381", {"start": v(-45.34, 1.77) * mm, "end": v(-44.54, 1.23) * mm});
            skLineSegment(sketch, "E382", {"start": v(-44.54, 1.23) * mm, "end": v(-44.85, 1.23) * mm});
            skLineSegment(sketch, "E383", {"start": v(-44.85, 1.23) * mm, "end": v(-46.2, 1.69) * mm});
            skLineSegment(sketch, "E384", {"start": v(-46.2, 1.69) * mm, "end": v(-47.3, 2.38) * mm});
            skLineSegment(sketch, "E385", {"start": v(-47.3, 2.38) * mm, "end": v(-47.3, 1.97) * mm});
            skLineSegment(sketch, "E386", {"start": v(-47.3, 1.97) * mm, "end": v(-45.28, 0.16) * mm});
            skLineSegment(sketch, "E387", {"start": v(-45.28, 0.16) * mm, "end": v(-44.25, -0.27) * mm});
            skLineSegment(sketch, "E388", {"start": v(-44.25, -0.27) * mm, "end": v(-44.57, -0.11) * mm});
            skLineSegment(sketch, "E389", {"start": v(-44.57, -0.11) * mm, "end": v(-44.25, -0.27) * mm});
            skLineSegment(sketch, "E390", {"start": v(-44.25, -0.27) * mm, "end": v(-43.9, -0.34) * mm});
            skLineSegment(sketch, "E391", {"start": v(-43.9, -0.34) * mm, "end": v(-43.49, -0.53) * mm});
            skLineSegment(sketch, "E392", {"start": v(-43.49, -0.53) * mm, "end": v(-41.97, -1.1) * mm});
            skLineSegment(sketch, "E393", {"start": v(-41.97, -1.1) * mm, "end": v(-40.17, -1.66) * mm});
            skLineSegment(sketch, "E394", {"start": v(-40.17, -1.66) * mm, "end": v(-38.12, -1.23) * mm});
            skLineSegment(sketch, "E395", {"start": v(-38.12, -1.23) * mm, "end": v(-35.86, 0.16) * mm});
            skLineSegment(sketch, "E396", {"start": v(-35.86, 0.16) * mm, "end": v(-36.06, -1.08) * mm});
            skLineSegment(sketch, "E397", {"start": v(-36.06, -1.08) * mm, "end": v(-35.72, -1.02) * mm});
            skLineSegment(sketch, "E398", {"start": v(-35.72, -1.02) * mm, "end": v(-34.56, -0.25) * mm});
            skLineSegment(sketch, "E399", {"start": v(-34.56, -0.25) * mm, "end": v(-33.76, -0.09) * mm});
            skLineSegment(sketch, "E400", {"start": v(-33.76, -0.09) * mm, "end": v(-33.8, -0.3) * mm});
            skLineSegment(sketch, "E401", {"start": v(-33.8, -0.3) * mm, "end": v(-34.24, -0.48) * mm});
            skLineSegment(sketch, "E402", {"start": v(-34.24, -0.48) * mm, "end": v(-35.02, -1.55) * mm});
            skLineSegment(sketch, "E403", {"start": v(-35.02, -1.55) * mm, "end": v(-35.63, -3.02) * mm});
            skLineSegment(sketch, "E404", {"start": v(-35.63, -3.02) * mm, "end": v(-35.72, -4.88) * mm});
            skLineSegment(sketch, "E405", {"start": v(-35.72, -4.88) * mm, "end": v(-35.55, -6.54) * mm});
            skLineSegment(sketch, "E406", {"start": v(-35.55, -6.54) * mm, "end": v(-35.98, -7.9) * mm});
            skLineSegment(sketch, "E407", {"start": v(-35.98, -7.9) * mm, "end": v(-36, -9.04) * mm});
            skLineSegment(sketch, "E408", {"start": v(-36, -9.04) * mm, "end": v(-35.44, -11.21) * mm});
            skLineSegment(sketch, "E409", {"start": v(-35.44, -11.21) * mm, "end": v(-35.35, -11.8) * mm});
            skLineSegment(sketch, "E410", {"start": v(-35.35, -11.8) * mm, "end": v(-35.6, -12.4) * mm});
            skLineSegment(sketch, "E411", {"start": v(-35.6, -12.4) * mm, "end": v(-35.49, -13.37) * mm});
            skLineSegment(sketch, "E412", {"start": v(-35.49, -13.37) * mm, "end": v(-34.8, -13.43) * mm});
            skLineSegment(sketch, "E413", {"start": v(-34.8, -13.43) * mm, "end": v(-34.32, -13) * mm});
            skLineSegment(sketch, "E414", {"start": v(-34.32, -13) * mm, "end": v(-34.03, -13.06) * mm});
            skLineSegment(sketch, "E415", {"start": v(-34.03, -13.06) * mm, "end": v(-33.85, -13.18) * mm});
            skLineSegment(sketch, "E416", {"start": v(-33.85, -13.18) * mm, "end": v(-33.23, -12.78) * mm});
            skLineSegment(sketch, "E417", {"start": v(-33.23, -12.78) * mm, "end": v(-33.35, -11.43) * mm});
            skLineSegment(sketch, "E418", {"start": v(-33.35, -11.43) * mm, "end": v(-34.96, -10.15) * mm});
            skLineSegment(sketch, "E419", {"start": v(-34.96, -10.15) * mm, "end": v(-35, -8.66) * mm});
            skLineSegment(sketch, "E420", {"start": v(-35, -8.66) * mm, "end": v(-33.96, -6.24) * mm});
            skLineSegment(sketch, "E421", {"start": v(-33.96, -6.24) * mm, "end": v(-33.47, -5.57) * mm});
            skLineSegment(sketch, "E422", {"start": v(-33.47, -5.57) * mm, "end": v(-33.3, -4.37) * mm});
            skLineSegment(sketch, "E423", {"start": v(-33.3, -4.37) * mm, "end": v(-33.77, -4.54) * mm});
            skLineSegment(sketch, "E424", {"start": v(-33.77, -4.54) * mm, "end": v(-34.33, -5.44) * mm});
            skLineSegment(sketch, "E425", {"start": v(-34.33, -5.44) * mm, "end": v(-34.61, -5.43) * mm});
            skLineSegment(sketch, "E426", {"start": v(-34.61, -5.43) * mm, "end": v(-33.8, -3.74) * mm});
            skLineSegment(sketch, "E427", {"start": v(-33.8, -3.74) * mm, "end": v(-33.3, -2.91) * mm});
            skLineSegment(sketch, "E428", {"start": v(-33.3, -2.91) * mm, "end": v(-32.2, -1.3) * mm});
            skLineSegment(sketch, "E429", {"start": v(-32.2, -1.3) * mm, "end": v(-32.14, 1.25) * mm});
            skLineSegment(sketch, "E430", {"start": v(-32.14, 1.25) * mm, "end": v(-33.1, 4.08) * mm});
            skLineSegment(sketch, "E431", {"start": v(-33.1, 4.08) * mm, "end": v(-33.28, 5.41) * mm});
            skLineSegment(sketch, "E432", {"start": v(-33.28, 5.41) * mm, "end": v(-32.76, 4.04) * mm});
            skLineSegment(sketch, "E433", {"start": v(-32.76, 4.04) * mm, "end": v(-31.7, 2.28) * mm});
            skLineSegment(sketch, "E434", {"start": v(-31.7, 2.28) * mm, "end": v(-31.1, 2.13) * mm});
            skLineSegment(sketch, "E435", {"start": v(-31.1, 2.13) * mm, "end": v(-30.6, 2.43) * mm});
            skLineSegment(sketch, "E436", {"start": v(-30.6, 2.43) * mm, "end": v(-30.17, 4.23) * mm});
            skLineSegment(sketch, "E437", {"start": v(-30.17, 4.23) * mm, "end": v(-29.92, 3.95) * mm});
            skLineSegment(sketch, "E438", {"start": v(-29.92, 3.95) * mm, "end": v(-29.86, 3.1) * mm});
            skLineSegment(sketch, "E439", {"start": v(-29.86, 3.1) * mm, "end": v(-29.4, 2.83) * mm});
            skLineSegment(sketch, "E440", {"start": v(-29.4, 2.83) * mm, "end": v(-28.87, 2.1) * mm});
            skLineSegment(sketch, "E441", {"start": v(-28.87, 2.1) * mm, "end": v(-27.72, 1.57) * mm});
            skLineSegment(sketch, "E442", {"start": v(-27.72, 1.57) * mm, "end": v(-28.2, 2.67) * mm});
            skLineSegment(sketch, "E443", {"start": v(-28.2, 2.67) * mm, "end": v(-26.45, 1.3) * mm});
            skLineSegment(sketch, "E444", {"start": v(-47.57, -11.95) * mm, "end": v(-45.38, -10.08) * mm});
            skLineSegment(sketch, "E445", {"start": v(-45.38, -10.08) * mm, "end": v(-45.12, -4.95) * mm});
            skLineSegment(sketch, "E446", {"start": v(-43.13, 14.23) * mm, "end": v(-41.79, 14.66) * mm});
            skLineSegment(sketch, "E447", {"start": v(-41.79, 14.66) * mm, "end": v(-39.56, 14.83) * mm});
            skLineSegment(sketch, "E448", {"start": v(-39.56, 14.83) * mm, "end": v(-37.14, 14.7) * mm});
            skLineSegment(sketch, "E449", {"start": v(-37.14, 14.7) * mm, "end": v(-35.88, 14.3) * mm});
            skLineSegment(sketch, "E450", {"start": v(-35.88, 14.3) * mm, "end": v(-35.33, 13.67) * mm});
            const initialGuessF0  = {"E1": [-0.01654, 0.006, 1, 0, 0.008], "E2": [-0.0094, -0.006, 1, 0, 0.006]};
            skSetInitialGuess(sketch, initialGuessF0);
            skSolve(sketch);
        }
        {
            var Q0;
            Q0=makeQuery(id+"F0.imprint","IMPRINT",FACE,{"disambiguationData":[TD([[makeQuery(id+"F0.imprint","IMPRINT",EDGE,{"derivedFrom":sQuery(id+"F0.wireOp",EDGE,"E0.bottom")}),1.0]])]});
            var Q1;
            Q1=makeQuery(id+"F0.imprint","IMPRINT",FACE,{"disambiguationData":[TD([[makeQuery(id+"F0.imprint","IMPRINT",EDGE,{"derivedFrom":sQuery(id+"F0.wireOp",EDGE,"E2.sketch_text.stroke-163")}),-1.0]])]});
            var Q2;
            Q2=makeQuery(id+"F0.imprint","IMPRINT",FACE,{"disambiguationData":[TD([[makeQuery(id+"F0.imprint","IMPRINT",EDGE,{"derivedFrom":sQuery(id+"F0.wireOp",EDGE,"E2.sketch_text.stroke-10")}),1.0]])]});
            var Q3;
            Q3=makeQuery(id+"F0.imprint","IMPRINT",FACE,{"disambiguationData":[TD([[makeQuery(id+"F0.imprint","IMPRINT",EDGE,{"derivedFrom":sQuery(id+"F0.wireOp",EDGE,"E1.sketch_text.stroke-60")}),1.0]])]});
            var Q4;
            Q4=makeQuery(id+"F0.imprint","IMPRINT",FACE,{"disambiguationData":[TD([[makeQuery(id+"F0.imprint","IMPRINT",EDGE,{"derivedFrom":sQuery(id+"F0.wireOp",EDGE,"E1.sketch_text.stroke-158")}),-1.0]])]});
            var Q5;
            Q5=makeQuery(id+"F0.imprint","IMPRINT",FACE,{"disambiguationData":[TD([[makeQuery(id+"F0.imprint","IMPRINT",EDGE,{"derivedFrom":sQuery(id+"F0.wireOp",EDGE,"E1.sketch_text.stroke-224")}),-1.0]])]});
            var Q6;
            Q6=makeQuery(id+"F0.imprint","IMPRINT",FACE,{"disambiguationData":[TD([[makeQuery(id+"F0.imprint","IMPRINT",EDGE,{"derivedFrom":sQuery(id+"F0.wireOp",EDGE,"E1.sketch_text.stroke-0")}),1.0]])]});
            var Q7;
            Q7=makeQuery(id+"F0.imprint","IMPRINT",FACE,{"disambiguationData":[TD([[makeQuery(id+"F0.imprint","IMPRINT",EDGE,{"derivedFrom":sQuery(id+"F0.wireOp",EDGE,"E1.sketch_text.stroke-123")}),-1.0]])]});
            var Q8;
            Q8=makeQuery(id+"F0.imprint","IMPRINT",FACE,{"disambiguationData":[TD([[makeQuery(id+"F0.imprint","IMPRINT",EDGE,{"derivedFrom":sQuery(id+"F0.wireOp",EDGE,"E1.sketch_text.stroke-214")}),1.0]])]});
            var Q9;
            Q9=makeQuery(id+"F0.imprint","IMPRINT",FACE,{"disambiguationData":[TD([[makeQuery(id+"F0.imprint","IMPRINT",EDGE,{"derivedFrom":sQuery(id+"F0.wireOp",EDGE,"E2.sketch_text.stroke-63")}),1.0]])]});
            var Q10;
            Q10=makeQuery(id+"F0.imprint","IMPRINT",FACE,{"disambiguationData":[TD([[makeQuery(id+"F0.imprint","IMPRINT",EDGE,{"derivedFrom":sQuery(id+"F0.wireOp",EDGE,"E2.sketch_text.stroke-227")}),-1.0]])]});
            var Q11;
            Q11=makeQuery(id+"F0.imprint","IMPRINT",FACE,{"disambiguationData":[TD([[makeQuery(id+"F0.imprint","IMPRINT",EDGE,{"derivedFrom":sQuery(id+"F0.wireOp",EDGE,"E1.sketch_text.stroke-38")}),-1.0]])]});
            var Q12;
            Q12=makeQuery(id+"F0.imprint","IMPRINT",FACE,{"disambiguationData":[TD([[makeQuery(id+"F0.imprint","IMPRINT",EDGE,{"derivedFrom":sQuery(id+"F0.wireOp",EDGE,"E1.sketch_text.stroke-178")}),-1.0]])]});
            var Q13;
            Q13=makeQuery(id+"F0.imprint","IMPRINT",FACE,{"disambiguationData":[TD([[makeQuery(id+"F0.imprint","IMPRINT",EDGE,{"derivedFrom":sQuery(id+"F0.wireOp",EDGE,"E2.sketch_text.stroke-71")}),-1.0]])]});
            var Q14;
            Q14=makeQuery(id+"F0.imprint","IMPRINT",FACE,{"disambiguationData":[TD([[makeQuery(id+"F0.imprint","IMPRINT",EDGE,{"derivedFrom":sQuery(id+"F0.wireOp",EDGE,"E1.sketch_text.stroke-12")}),-1.0]])]});
            var Q15;
            Q15=makeQuery(id+"F0.imprint","IMPRINT",FACE,{"disambiguationData":[TD([[makeQuery(id+"F0.imprint","IMPRINT",EDGE,{"derivedFrom":sQuery(id+"F0.wireOp",EDGE,"E1.sketch_text.stroke-115")}),1.0]])]});
            var Q16;
            Q16=makeQuery(id+"F0.imprint","IMPRINT",FACE,{"disambiguationData":[TD([[makeQuery(id+"F0.imprint","IMPRINT",EDGE,{"derivedFrom":sQuery(id+"F0.wireOp",EDGE,"E2.sketch_text.stroke-202")}),-1.0]])]});
            var Q17;
            Q17=makeQuery(id+"F0.imprint","IMPRINT",FACE,{"disambiguationData":[TD([[makeQuery(id+"F0.imprint","IMPRINT",EDGE,{"derivedFrom":sQuery(id+"F0.wireOp",EDGE,"E2.sketch_text.stroke-104")}),-1.0]])]});
            var Q18;
            Q18=makeQuery(id+"F0.imprint","IMPRINT",FACE,{"disambiguationData":[TD([[makeQuery(id+"F0.imprint","IMPRINT",EDGE,{"derivedFrom":sQuery(id+"F0.wireOp",EDGE,"E2.sketch_text.stroke-97")}),1.0]])]});
            var Q19;
            Q19=makeQuery(id+"F0.imprint","IMPRINT",FACE,{"disambiguationData":[TD([[makeQuery(id+"F0.imprint","IMPRINT",EDGE,{"derivedFrom":sQuery(id+"F0.wireOp",EDGE,"E2.sketch_text.stroke-217")}),1.0]])]});
            var Q20;
            Q20=makeQuery(id+"F0.imprint","IMPRINT",FACE,{"disambiguationData":[TD([[makeQuery(id+"F0.imprint","IMPRINT",EDGE,{"derivedFrom":sQuery(id+"F0.wireOp",EDGE,"E1.sketch_text.stroke-168")}),1.0]])]});
            var Q21;
            Q21=makeQuery(id+"F0.imprint","IMPRINT",FACE,{"disambiguationData":[TD([[makeQuery(id+"F0.imprint","IMPRINT",EDGE,{"derivedFrom":sQuery(id+"F0.wireOp",EDGE,"E1.sketch_text.stroke-142")}),-1.0]])]});
            var Q22;
            Q22=makeQuery(id+"F0.imprint","IMPRINT",FACE,{"disambiguationData":[TD([[makeQuery(id+"F0.imprint","IMPRINT",EDGE,{"derivedFrom":sQuery(id+"F0.wireOp",EDGE,"E1.sketch_text.stroke-0")}),-1.0]])]});
            var Q23;
            Q23=makeQuery(id+"F0.imprint","IMPRINT",FACE,{"disambiguationData":[TD([[makeQuery(id+"F0.imprint","IMPRINT",EDGE,{"derivedFrom":sQuery(id+"F0.wireOp",EDGE,"E2.sketch_text.stroke-121")}),-1.0]])]});
            var Q24;
            Q24=makeQuery(id+"F0.imprint","IMPRINT",FACE,{"disambiguationData":[TD([[makeQuery(id+"F0.imprint","IMPRINT",EDGE,{"derivedFrom":sQuery(id+"F0.wireOp",EDGE,"E1.sketch_text.stroke-204")}),-1.0]])]});
            var Q25;
            Q25=makeQuery(id+"F0.imprint","IMPRINT",FACE,{"disambiguationData":[TD([[makeQuery(id+"F0.imprint","IMPRINT",EDGE,{"derivedFrom":sQuery(id+"F0.wireOp",EDGE,"E1.sketch_text.stroke-88")}),-1.0]])]});
            var Q26;
            Q26=makeQuery(id+"F0.imprint","IMPRINT",FACE,{"disambiguationData":[TD([[makeQuery(id+"F0.imprint","IMPRINT",EDGE,{"derivedFrom":sQuery(id+"F0.wireOp",EDGE,"E1.sketch_text.stroke-248")}),-1.0]])]});
            var Q27;
            Q27=makeQuery(id+"F0.imprint","IMPRINT",FACE,{"disambiguationData":[TD([[makeQuery(id+"F0.imprint","IMPRINT",EDGE,{"derivedFrom":sQuery(id+"F0.wireOp",EDGE,"E2.sketch_text.stroke-79")}),-1.0]])]});
            var Q28;
            Q28=makeQuery(id+"F0.imprint","IMPRINT",FACE,{"disambiguationData":[TD([[makeQuery(id+"F0.imprint","IMPRINT",EDGE,{"derivedFrom":sQuery(id+"F0.wireOp",EDGE,"E2.sketch_text.stroke-0")}),-1.0]])]});
            var Q29;
            Q29=makeQuery(id+"F0.imprint","IMPRINT",FACE,{"disambiguationData":[TD([[makeQuery(id+"F0.imprint","IMPRINT",EDGE,{"derivedFrom":sQuery(id+"F0.wireOp",EDGE,"E2.sketch_text.stroke-25")}),1.0]])]});
            var Q30;
            Q30=makeQuery(id+"F0.imprint","IMPRINT",FACE,{"disambiguationData":[TD([[makeQuery(id+"F0.imprint","IMPRINT",EDGE,{"derivedFrom":sQuery(id+"F0.wireOp",EDGE,"E1.sketch_text.stroke-70")}),-1.0]])]});
            var Q31;
            Q31=makeQuery(id+"F0.imprint","IMPRINT",FACE,{"disambiguationData":[TD([[makeQuery(id+"F0.imprint","IMPRINT",EDGE,{"derivedFrom":sQuery(id+"F0.wireOp",EDGE,"E2.sketch_text.stroke-143")}),-1.0]])]});
            var Q32;
            Q32=makeQuery(id+"F0.imprint","IMPRINT",FACE,{"disambiguationData":[TD([[makeQuery(id+"F0.imprint","IMPRINT",EDGE,{"derivedFrom":sQuery(id+"F0.wireOp",EDGE,"E2.sketch_text.stroke-191")}),-1.0]])]});
            var Q33;
            Q33=makeQuery(id+"F0.imprint","IMPRINT",FACE,{"disambiguationData":[TD([[makeQuery(id+"F0.imprint","IMPRINT",EDGE,{"derivedFrom":sQuery(id+"F0.wireOp",EDGE,"E2.sketch_text.stroke-55")}),-1.0]])]});
            var Q34;
            Q34=makeQuery(id+"F0.imprint","IMPRINT",FACE,{"disambiguationData":[TD([[makeQuery(id+"F0.imprint","IMPRINT",EDGE,{"derivedFrom":sQuery(id+"F0.wireOp",EDGE,"E2.sketch_text.stroke-17")}),1.0]])]});
            var Q35;
            Q35=makeQuery(id+"F0.imprint","IMPRINT",FACE,{"disambiguationData":[TD([[makeQuery(id+"F0.imprint","IMPRINT",EDGE,{"derivedFrom":sQuery(id+"F0.wireOp",EDGE,"E2.sketch_text.stroke-17")}),-1.0]])]});
            var Q36;
            Q36=makeQuery(id+"F0.imprint","IMPRINT",FACE,{"disambiguationData":[TD([[makeQuery(id+"F0.imprint","IMPRINT",EDGE,{"derivedFrom":sQuery(id+"F0.wireOp",EDGE,"E2.sketch_text.stroke-174")}),-1.0]])]});
            var Q37;
            Q37=makeQuery(id+"F0.imprint","IMPRINT",FACE,{"disambiguationData":[TD([[makeQuery(id+"F0.imprint","IMPRINT",EDGE,{"derivedFrom":sQuery(id+"F0.wireOp",EDGE,"E2.sketch_text.stroke-195")}),-1.0]])]});
            var Q38;
            Q38=makeQuery(id+"F0.imprint","IMPRINT",FACE,{"disambiguationData":[TD([[makeQuery(id+"F0.imprint","IMPRINT",EDGE,{"derivedFrom":sQuery(id+"F0.wireOp",EDGE,"E2.sketch_text.stroke-167")}),-1.0]])]});
            var Q39;
            Q39=makeQuery(id+"F0.imprint","IMPRINT",FACE,{"disambiguationData":[TD([[makeQuery(id+"F0.imprint","IMPRINT",EDGE,{"derivedFrom":sQuery(id+"F0.wireOp",EDGE,"E4")}),-1.0]])]});
            var Q40;
            Q40=makeQuery(id+"F0.imprint","IMPRINT",FACE,{"disambiguationData":[TD([[makeQuery(id+"F0.imprint","IMPRINT",EDGE,{"derivedFrom":sQuery(id+"F0.wireOp",EDGE,"E94")}),-1.0]])]});
            var Q41;
            Q41=makeQuery(id+"F0.imprint","IMPRINT",FACE,{"disambiguationData":[TD([[makeQuery(id+"F0.imprint","IMPRINT",EDGE,{"derivedFrom":sQuery(id+"F0.wireOp",EDGE,"E96")}),1.0]])]});
            var Q42;
            Q42=makeQuery(id+"F0.imprint","IMPRINT",FACE,{"disambiguationData":[TD([[makeQuery(id+"F0.imprint","IMPRINT",EDGE,{"derivedFrom":sQuery(id+"F0.wireOp",EDGE,"E139")}),1.0]])]});
            var Q43;
            Q43=makeQuery(id+"F0.imprint","IMPRINT",FACE,{"disambiguationData":[TD([[makeQuery(id+"F0.imprint","IMPRINT",EDGE,{"derivedFrom":sQuery(id+"F0.wireOp",EDGE,"E127")}),1.0]])]});
            var Q44;
            Q44=makeQuery(id+"F0.imprint","IMPRINT",FACE,{"disambiguationData":[TD([[makeQuery(id+"F0.imprint","IMPRINT",EDGE,{"derivedFrom":sQuery(id+"F0.wireOp",EDGE,"E150")}),-1.0]])]});
            var Q45;
            Q45=makeQuery(id+"F0.imprint","IMPRINT",FACE,{"disambiguationData":[TD([[makeQuery(id+"F0.imprint","IMPRINT",EDGE,{"derivedFrom":sQuery(id+"F0.wireOp",EDGE,"E270")}),1.0]])]});
            var Q46;
            Q46=makeQuery(id+"F0.imprint","IMPRINT",FACE,{"disambiguationData":[TD([[makeQuery(id+"F0.imprint","IMPRINT",EDGE,{"derivedFrom":sQuery(id+"F0.wireOp",EDGE,"E264")}),1.0]])]});
            var Q47;
            Q47=makeQuery(id+"F0.imprint","IMPRINT",FACE,{"disambiguationData":[TD([[makeQuery(id+"F0.imprint","IMPRINT",EDGE,{"derivedFrom":sQuery(id+"F0.wireOp",EDGE,"E280")}),1.0]])]});
            var Q48;
            Q48=makeQuery(id+"F0.imprint","IMPRINT",FACE,{"disambiguationData":[TD([[makeQuery(id+"F0.imprint","IMPRINT",EDGE,{"derivedFrom":sQuery(id+"F0.wireOp",EDGE,"E194")}),1.0]])]});
            var Q49;
            Q49=makeQuery(id+"F0.imprint","IMPRINT",FACE,{"disambiguationData":[TD([[makeQuery(id+"F0.imprint","IMPRINT",EDGE,{"derivedFrom":sQuery(id+"F0.wireOp",EDGE,"E171")}),1.0]])]});
            var Q50;
            Q50=makeQuery(id+"F0.imprint","IMPRINT",FACE,{"disambiguationData":[TD([[makeQuery(id+"F0.imprint","IMPRINT",EDGE,{"derivedFrom":sQuery(id+"F0.wireOp",EDGE,"E183")}),-1.0]])]});
            extrude(context, id + "F1", {"entities" : qUnion([Q0, Q1, Q2, Q3, Q4, Q5, Q6, Q7, Q8, Q9, Q10, Q11, Q12, Q13, Q14, Q15, Q16, Q17, Q18, Q19, Q20, Q21, Q22, Q23, Q24, Q25, Q26, Q27, Q28, Q29, Q30, Q31, Q32, Q33, Q34, Q35, Q36, Q37, Q38, Q39, Q40, Q41, Q42, Q43, Q44, Q45, Q46, Q47, Q48, Q49, Q50]), "oppositeDirection" : true, "depth" : 1 * mm, "offsetDistance" : 25 * mm});
        }
        {
            var Q0;
            Q0=makeQuery(id+"F0.imprint","IMPRINT",FACE,{"disambiguationData":[TD([[makeQuery(id+"F0.imprint","IMPRINT",EDGE,{"derivedFrom":sQuery(id+"F0.wireOp",EDGE,"E1.sketch_text.stroke-0")}),-1.0]])]});
            var Q1;
            Q1=makeQuery(id+"F0.imprint","IMPRINT",FACE,{"disambiguationData":[TD([[makeQuery(id+"F0.imprint","IMPRINT",EDGE,{"derivedFrom":sQuery(id+"F0.wireOp",EDGE,"E1.sketch_text.stroke-12")}),-1.0]])]});
            var Q2;
            Q2=makeQuery(id+"F0.imprint","IMPRINT",FACE,{"disambiguationData":[TD([[makeQuery(id+"F0.imprint","IMPRINT",EDGE,{"derivedFrom":sQuery(id+"F0.wireOp",EDGE,"E1.sketch_text.stroke-38")}),-1.0]])]});
            var Q3;
            Q3=makeQuery(id+"F0.imprint","IMPRINT",FACE,{"disambiguationData":[TD([[makeQuery(id+"F0.imprint","IMPRINT",EDGE,{"derivedFrom":sQuery(id+"F0.wireOp",EDGE,"E1.sketch_text.stroke-70")}),-1.0]])]});
            var Q4;
            Q4=makeQuery(id+"F0.imprint","IMPRINT",FACE,{"disambiguationData":[TD([[makeQuery(id+"F0.imprint","IMPRINT",EDGE,{"derivedFrom":sQuery(id+"F0.wireOp",EDGE,"E1.sketch_text.stroke-88")}),-1.0]])]});
            var Q5;
            Q5=makeQuery(id+"F0.imprint","IMPRINT",FACE,{"disambiguationData":[TD([[makeQuery(id+"F0.imprint","IMPRINT",EDGE,{"derivedFrom":sQuery(id+"F0.wireOp",EDGE,"E1.sketch_text.stroke-123")}),-1.0]])]});
            var Q6;
            Q6=makeQuery(id+"F0.imprint","IMPRINT",FACE,{"disambiguationData":[TD([[makeQuery(id+"F0.imprint","IMPRINT",EDGE,{"derivedFrom":sQuery(id+"F0.wireOp",EDGE,"E1.sketch_text.stroke-142")}),-1.0]])]});
            var Q7;
            Q7=makeQuery(id+"F0.imprint","IMPRINT",FACE,{"disambiguationData":[TD([[makeQuery(id+"F0.imprint","IMPRINT",EDGE,{"derivedFrom":sQuery(id+"F0.wireOp",EDGE,"E1.sketch_text.stroke-158")}),-1.0]])]});
            var Q8;
            Q8=makeQuery(id+"F0.imprint","IMPRINT",FACE,{"disambiguationData":[TD([[makeQuery(id+"F0.imprint","IMPRINT",EDGE,{"derivedFrom":sQuery(id+"F0.wireOp",EDGE,"E1.sketch_text.stroke-178")}),-1.0]])]});
            var Q9;
            Q9=makeQuery(id+"F0.imprint","IMPRINT",FACE,{"disambiguationData":[TD([[makeQuery(id+"F0.imprint","IMPRINT",EDGE,{"derivedFrom":sQuery(id+"F0.wireOp",EDGE,"E1.sketch_text.stroke-204")}),-1.0]])]});
            var Q10;
            Q10=makeQuery(id+"F0.imprint","IMPRINT",FACE,{"disambiguationData":[TD([[makeQuery(id+"F0.imprint","IMPRINT",EDGE,{"derivedFrom":sQuery(id+"F0.wireOp",EDGE,"E1.sketch_text.stroke-224")}),-1.0]])]});
            var Q11;
            Q11=makeQuery(id+"F0.imprint","IMPRINT",FACE,{"disambiguationData":[TD([[makeQuery(id+"F0.imprint","IMPRINT",EDGE,{"derivedFrom":sQuery(id+"F0.wireOp",EDGE,"E1.sketch_text.stroke-248")}),-1.0]])]});
            var Q12;
            Q12=makeQuery(id+"F0.imprint","IMPRINT",FACE,{"disambiguationData":[TD([[makeQuery(id+"F0.imprint","IMPRINT",EDGE,{"derivedFrom":sQuery(id+"F0.wireOp",EDGE,"E2.sketch_text.stroke-227")}),-1.0]])]});
            var Q13;
            Q13=makeQuery(id+"F0.imprint","IMPRINT",FACE,{"disambiguationData":[TD([[makeQuery(id+"F0.imprint","IMPRINT",EDGE,{"derivedFrom":sQuery(id+"F0.wireOp",EDGE,"E2.sketch_text.stroke-202")}),-1.0]])]});
            var Q14;
            Q14=makeQuery(id+"F0.imprint","IMPRINT",FACE,{"disambiguationData":[TD([[makeQuery(id+"F0.imprint","IMPRINT",EDGE,{"derivedFrom":sQuery(id+"F0.wireOp",EDGE,"E2.sketch_text.stroke-191")}),-1.0]])]});
            var Q15;
            Q15=makeQuery(id+"F0.imprint","IMPRINT",FACE,{"disambiguationData":[TD([[makeQuery(id+"F0.imprint","IMPRINT",EDGE,{"derivedFrom":sQuery(id+"F0.wireOp",EDGE,"E2.sketch_text.stroke-195")}),-1.0]])]});
            var Q16;
            Q16=makeQuery(id+"F0.imprint","IMPRINT",FACE,{"disambiguationData":[TD([[makeQuery(id+"F0.imprint","IMPRINT",EDGE,{"derivedFrom":sQuery(id+"F0.wireOp",EDGE,"E2.sketch_text.stroke-174")}),-1.0]])]});
            var Q17;
            Q17=makeQuery(id+"F0.imprint","IMPRINT",FACE,{"disambiguationData":[TD([[makeQuery(id+"F0.imprint","IMPRINT",EDGE,{"derivedFrom":sQuery(id+"F0.wireOp",EDGE,"E2.sketch_text.stroke-163")}),-1.0]])]});
            var Q18;
            Q18=makeQuery(id+"F0.imprint","IMPRINT",FACE,{"disambiguationData":[TD([[makeQuery(id+"F0.imprint","IMPRINT",EDGE,{"derivedFrom":sQuery(id+"F0.wireOp",EDGE,"E2.sketch_text.stroke-167")}),-1.0]])]});
            var Q19;
            Q19=makeQuery(id+"F0.imprint","IMPRINT",FACE,{"disambiguationData":[TD([[makeQuery(id+"F0.imprint","IMPRINT",EDGE,{"derivedFrom":sQuery(id+"F0.wireOp",EDGE,"E2.sketch_text.stroke-143")}),-1.0]])]});
            var Q20;
            Q20=makeQuery(id+"F0.imprint","IMPRINT",FACE,{"disambiguationData":[TD([[makeQuery(id+"F0.imprint","IMPRINT",EDGE,{"derivedFrom":sQuery(id+"F0.wireOp",EDGE,"E2.sketch_text.stroke-121")}),-1.0]])]});
            var Q21;
            Q21=makeQuery(id+"F0.imprint","IMPRINT",FACE,{"disambiguationData":[TD([[makeQuery(id+"F0.imprint","IMPRINT",EDGE,{"derivedFrom":sQuery(id+"F0.wireOp",EDGE,"E2.sketch_text.stroke-104")}),-1.0]])]});
            var Q22;
            Q22=makeQuery(id+"F0.imprint","IMPRINT",FACE,{"disambiguationData":[TD([[makeQuery(id+"F0.imprint","IMPRINT",EDGE,{"derivedFrom":sQuery(id+"F0.wireOp",EDGE,"E2.sketch_text.stroke-79")}),-1.0]])]});
            var Q23;
            Q23=makeQuery(id+"F0.imprint","IMPRINT",FACE,{"disambiguationData":[TD([[makeQuery(id+"F0.imprint","IMPRINT",EDGE,{"derivedFrom":sQuery(id+"F0.wireOp",EDGE,"E2.sketch_text.stroke-71")}),-1.0]])]});
            var Q24;
            Q24=makeQuery(id+"F0.imprint","IMPRINT",FACE,{"disambiguationData":[TD([[makeQuery(id+"F0.imprint","IMPRINT",EDGE,{"derivedFrom":sQuery(id+"F0.wireOp",EDGE,"E2.sketch_text.stroke-0")}),-1.0]])]});
            var Q25;
            Q25=makeQuery(id+"F0.imprint","IMPRINT",FACE,{"disambiguationData":[TD([[makeQuery(id+"F0.imprint","IMPRINT",EDGE,{"derivedFrom":sQuery(id+"F0.wireOp",EDGE,"E2.sketch_text.stroke-17")}),-1.0]])]});
            var Q26;
            Q26=makeQuery(id+"F0.imprint","IMPRINT",FACE,{"disambiguationData":[TD([[makeQuery(id+"F0.imprint","IMPRINT",EDGE,{"derivedFrom":sQuery(id+"F0.wireOp",EDGE,"E2.sketch_text.stroke-55")}),-1.0]])]});
            var Q27;
            Q27=makeQuery(id+"F0.imprint","IMPRINT",FACE,{"disambiguationData":[TD([[makeQuery(id+"F0.imprint","IMPRINT",EDGE,{"derivedFrom":sQuery(id+"F0.wireOp",EDGE,"E0.bottom")}),1.0]])]});
            var Q28;
            Q28=makeQuery(id+"F0.imprint","IMPRINT",FACE,{"disambiguationData":[TD([[makeQuery(id+"F0.imprint","IMPRINT",EDGE,{"derivedFrom":sQuery(id+"F0.wireOp",EDGE,"E4")}),-1.0]])]});
            extrude(context, id + "F2", {"entities" : qUnion([Q0, Q1, Q2, Q3, Q4, Q5, Q6, Q7, Q8, Q9, Q10, Q11, Q12, Q13, Q14, Q15, Q16, Q17, Q18, Q19, Q20, Q21, Q22, Q23, Q24, Q25, Q26, Q27, Q28]), "operationType" : NewBodyOperationType.ADD, "depth" : 1 * mm, "offsetDistance" : 25 * mm});
        }
    });